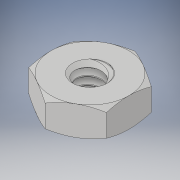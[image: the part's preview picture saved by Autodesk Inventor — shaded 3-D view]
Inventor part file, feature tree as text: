
AUTODESK INVENTOR PART (.ipt)
format: ipt  version: 2019 (Build 230136000, 136)  size: 254,464 bytes
history: native  units: in
note: dims shown in document units (in); Inventor stores cm internally (conversion verified against a paired STEP export)
features: mirror x1
ambient origin geometry x8: Origin, YZ Plane, XZ Plane, XY Plane, X Axis, Y Axis, Z Axis, Center Point
bodies: Solid1 (feature_tree)
feature tree (1):
  mirror  "Mirror1"
